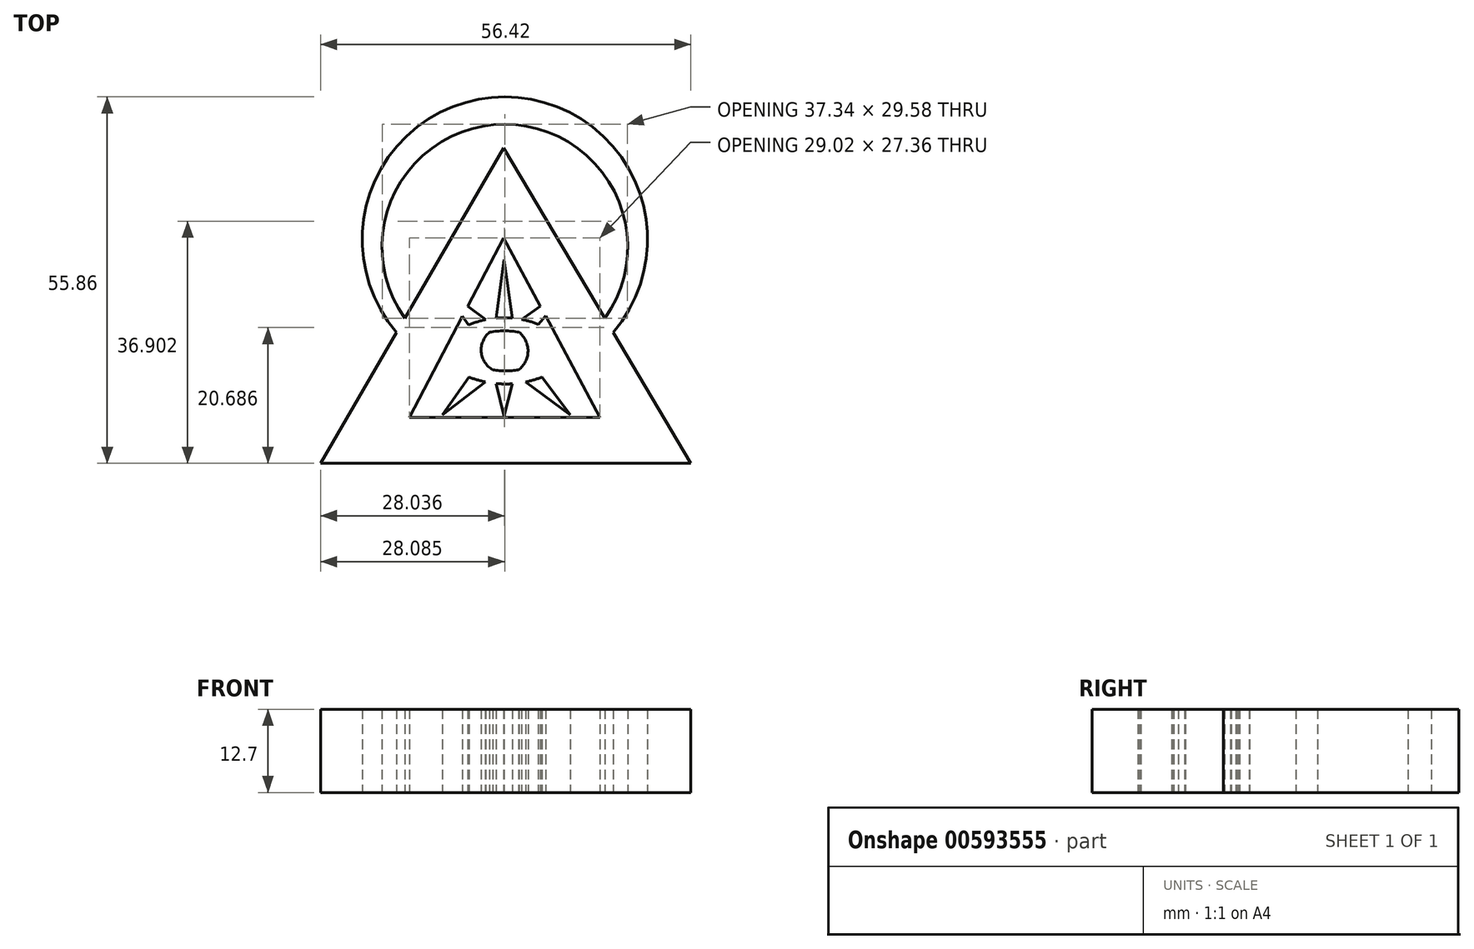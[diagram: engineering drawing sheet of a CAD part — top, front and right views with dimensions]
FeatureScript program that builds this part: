
annotation { "Feature Type Name" : "Feature", "Feature Type Description" : "" }
export const myFeature = defineFeature(function(context is Context, id is Id, definition is map)
    precondition{}
    {
        {
            var Q0;
            Q0=qCreatedBy(makeId("Top.planeOp"),FACE);
            var sketch = newSketch(context, id + "F0", { "sketchPlane" : qUnion([Q0])});
            skLineSegment(sketch, "E0", {"start": v(0, 38.6) * mm, "end": v(0, -34.74) * mm, "construction": true});
            skPoint(sketch, "E1", {"position": v(-16.4, 0.56) * mm});
            skPoint(sketch, "E2", {"position": v(16.6, 0.56) * mm});
            skArc(sketch, "E3", {"start": v(16.6, 0.56) * mm, "mid": v(0.1, 36.45) * mm, "end": v(-16.4, 0.56) * mm});
            skPoint(sketch, "E4", {"position": v(-15.15, 2.7) * mm});
            skPoint(sketch, "E5", {"position": v(15.34, 2.7) * mm});
            skArc(sketch, "E6", {"start": v(15.34, 2.7) * mm, "mid": v(0.1, 32.28) * mm, "end": v(-15.15, 2.7) * mm});
            skPoint(sketch, "E7", {"position": v(-28, -19.4) * mm});
            skPoint(sketch, "E8", {"position": v(28.43, -19.4) * mm});
            skPoint(sketch, "E9", {"position": v(-0.05, 28.7) * mm});
            skLineSegment(sketch, "E10", {"start": v(-28, -19.4) * mm, "end": v(-0.05, 28.7) * mm});
            skLineSegment(sketch, "E11", {"start": v(28.43, -19.4) * mm, "end": v(-0.05, 28.7) * mm});
            skLineSegment(sketch, "E12", {"start": v(-28, -19.4) * mm, "end": v(28.43, -19.4) * mm});
            skPoint(sketch, "E13", {"position": v(-0.05, 14.96) * mm});
            skPoint(sketch, "E14", {"position": v(-14.46, -12.4) * mm});
            skLineSegment(sketch, "E15", {"start": v(-0.05, 14.96) * mm, "end": v(-14.46, -12.4) * mm});
            skPoint(sketch, "E16", {"position": v(14.56, -12.4) * mm});
            skLineSegment(sketch, "E17", {"start": v(-14.46, -12.4) * mm, "end": v(14.56, -12.4) * mm});
            skLineSegment(sketch, "E18", {"start": v(-0.05, 14.96) * mm, "end": v(14.56, -12.4) * mm});
            skLineSegment(sketch, "E19", {"start": v(-0.05, 28.7) * mm, "end": v(-0.05, 14.96) * mm, "construction": true});
            skLineSegment(sketch, "E20", {"start": v(-23.93, -12.4) * mm, "end": v(24.29, -12.4) * mm, "construction": true});
            skArc(sketch, "E21", {"start": v(-9.81, -3.57) * mm, "mid": v(0.03, -7.32) * mm, "end": v(9.97, -3.8) * mm});
            skArc(sketch, "E22", {"start": v(7.68, 0.48) * mm, "mid": v(0, 2.77) * mm, "end": v(-7.68, 0.48) * mm});
            skArc(sketch, "E23", {"start": v(-8.17, -2.18) * mm, "mid": v(0.1, -5.32) * mm, "end": v(8.43, -2.36) * mm});
            skArc(sketch, "E24", {"start": v(8.43, -2.36) * mm, "mid": v(0.16, 0.77) * mm, "end": v(-8.17, -2.18) * mm});
            skPoint(sketch, "E25", {"position": v(-1.72, -5.17) * mm});
            skPoint(sketch, "E26", {"position": v(2.2, -5.17) * mm});
            skPoint(sketch, "E27", {"position": v(2.27, 0.58) * mm});
            skArc(sketch, "E28", {"start": v(-2.22, 0.58) * mm, "mid": v(-3.49, -2.43) * mm, "end": v(-1.72, -5.17) * mm});
            skPoint(sketch, "E29", {"position": v(-2.22, 0.58) * mm});
            skArc(sketch, "E30", {"start": v(2.2, -5.17) * mm, "mid": v(3.63, -2.32) * mm, "end": v(2.27, 0.58) * mm});
            skLineSegment(sketch, "E31", {"start": v(-2.88, -7) * mm, "end": v(-9.45, -12.05) * mm});
            skLineSegment(sketch, "E32", {"start": v(-9.45, -12.05) * mm, "end": v(-5.38, -6.26) * mm});
            skLineSegment(sketch, "E33", {"start": v(3.3, -7) * mm, "end": v(10.06, -12.01) * mm});
            skLineSegment(sketch, "E34", {"start": v(10.06, -12.01) * mm, "end": v(5.8, -6.27) * mm});
            skLineSegment(sketch, "E35", {"start": v(-6.35, 3) * mm, "end": v(-5.42, 1.68) * mm});
            skLineSegment(sketch, "E36", {"start": v(-5.53, 4.55) * mm, "end": v(-2.82, 2.49) * mm});
            skLineSegment(sketch, "E37", {"start": v(-1.25, 2.72) * mm, "end": v(0, 11.63) * mm});
            skLineSegment(sketch, "E38", {"start": v(0, 11.63) * mm, "end": v(1.25, 2.72) * mm});
            skLineSegment(sketch, "E39", {"start": v(2.67, 2.52) * mm, "end": v(5.51, 4.53) * mm});
            skLineSegment(sketch, "E40", {"start": v(6.3, 3.05) * mm, "end": v(5.21, 1.77) * mm});
            skLineSegment(sketch, "E41", {"start": v(-7.68, 0.48) * mm, "end": v(-9.81, -3.57) * mm});
            skLineSegment(sketch, "E42", {"start": v(-6.35, 3) * mm, "end": v(-5.53, 4.55) * mm});
            skLineSegment(sketch, "E43", {"start": v(7.68, 0.48) * mm, "end": v(9.97, -3.8) * mm});
            skLineSegment(sketch, "E44", {"start": v(5.51, 4.53) * mm, "end": v(6.3, 3.05) * mm});
            skArc(sketch, "E45", {"start": v(2.27, 0.58) * mm, "mid": v(0.03, 0.77) * mm, "end": v(-2.22, 0.58) * mm});
            skLineSegment(sketch, "E46", {"start": v(-1.25, -7.25) * mm, "end": v(0, -12.25) * mm});
            skLineSegment(sketch, "E47", {"start": v(0, -12.25) * mm, "end": v(1.25, -7.29) * mm});
            skLineSegment(sketch, "E48", {"start": v(0, -12.25) * mm, "end": v(-1.25, -7.25) * mm, "construction": true});
            skLineSegment(sketch, "E49", {"start": v(-1.25, 2.72) * mm, "end": v(-1.25, -9.07) * mm, "construction": true});
            skLineSegment(sketch, "E50", {"start": v(1.25, 2.72) * mm, "end": v(1.25, -9.05) * mm, "construction": true});
            skSolve(sketch);
        }
        {
            var Q0;
            Q0 = qSketchRegion(id + "F0", true);
            var Q1;
            {var subQ0=sQuery(id+"F0.wireOp",EDGE,"E28");Q1=makeQuery(id+"F0.imprint","IMPRINT",FACE,{"disambiguationData":[TD([[makeQuery(id+"F0.imprint","IMPRINT",EDGE,{"derivedFrom":subQ0}),1.0]])]});}
            var Q2;
            {var subQ10=sQuery(id+"F0.wireOp",EDGE,"E41");Q2=makeQuery(id+"F0.imprint","IMPRINT",FACE,{"disambiguationData":[TD([[makeQuery(id+"F0.imprint","IMPRINT",EDGE,{"derivedFrom":subQ10}),1.0]])]});}
            var Q3;
            {var subQ0=sQuery(id+"F0.wireOp",EDGE,"E35");Q3=makeQuery(id+"F0.imprint","IMPRINT",FACE,{"disambiguationData":[TD([[makeQuery(id+"F0.imprint","IMPRINT",EDGE,{"derivedFrom":subQ0}),1.0]])]});}
            var Q4;
            {var subQ0=sQuery(id+"F0.wireOp",EDGE,"E37");Q4=makeQuery(id+"F0.imprint","IMPRINT",FACE,{"disambiguationData":[TD([[makeQuery(id+"F0.imprint","IMPRINT",EDGE,{"derivedFrom":subQ0}),-1.0]])]});}
            var Q5;
            {var subQ0=sQuery(id+"F0.wireOp",EDGE,"E39");Q5=makeQuery(id+"F0.imprint","IMPRINT",FACE,{"disambiguationData":[TD([[makeQuery(id+"F0.imprint","IMPRINT",EDGE,{"derivedFrom":subQ0}),-1.0]])]});}
            var Q6;
            {var subQ0=sQuery(id+"F0.wireOp",EDGE,"E31");Q6=makeQuery(id+"F0.imprint","IMPRINT",FACE,{"disambiguationData":[TD([[makeQuery(id+"F0.imprint","IMPRINT",EDGE,{"derivedFrom":subQ0}),-1.0]])]});}
            var Q7;
            {var subQ0=sQuery(id+"F0.wireOp",EDGE,"E33");Q7=makeQuery(id+"F0.imprint","IMPRINT",FACE,{"disambiguationData":[TD([[makeQuery(id+"F0.imprint","IMPRINT",EDGE,{"derivedFrom":subQ0}),1.0]])]});}
            var Q8;
            {var subQ0=sQuery(id+"F0.wireOp",EDGE,"E46");Q8=makeQuery(id+"F0.imprint","IMPRINT",FACE,{"disambiguationData":[TD([[makeQuery(id+"F0.imprint","IMPRINT",EDGE,{"derivedFrom":subQ0}),1.0]])]});}
            var Q9;
            Q9=sQuery(id+"F0.wireOp",EDGE,"E3");
            var Q10;
            Q10=sQuery(id+"F0.wireOp",EDGE,"E6");
            var Q11;
            Q11=sQuery(id+"F0.wireOp",EDGE,"E10");
            var Q12;
            Q12=sQuery(id+"F0.wireOp",EDGE,"E12");
            var Q13;
            Q13=sQuery(id+"F0.wireOp",EDGE,"E17");
            var Q14;
            Q14=sQuery(id+"F0.wireOp",EDGE,"E15");
            var Q15;
            Q15=sQuery(id+"F0.wireOp",EDGE,"E18");
            var Q16;
            Q16=sQuery(id+"F0.wireOp",EDGE,"E11");
            var Q17;
            Q17=sQuery(id+"F0.wireOp",EDGE,"E31");
            var Q18;
            Q18=sQuery(id+"F0.wireOp",EDGE,"E32");
            var Q19;
            Q19=sQuery(id+"F0.wireOp",EDGE,"cENFgDZo-e2X2-sVkA-bZeN-yT4mE3rmpJwd");
            var Q20;
            Q20=sQuery(id+"F0.wireOp",EDGE,"vWQVmkAs-JZlU-UwJa-lEx6-7OVIaMs9nSNG");
            var Q21;
            Q21=sQuery(id+"F0.wireOp",EDGE,"E33");
            var Q22;
            Q22=sQuery(id+"F0.wireOp",EDGE,"E34");
            var Q23;
            Q23=sQuery(id+"F0.wireOp",EDGE,"E21");
            var Q24;
            Q24=sQuery(id+"F0.wireOp",EDGE,"E23");
            var Q25;
            Q25=sQuery(id+"F0.wireOp",EDGE,"E30");
            var Q26;
            Q26=sQuery(id+"F0.wireOp",EDGE,"E28");
            var Q27;
            Q27=sQuery(id+"F0.wireOp",EDGE,"E24");
            var Q28;
            Q28=sQuery(id+"F0.wireOp",EDGE,"E35");
            var Q29;
            Q29=sQuery(id+"F0.wireOp",EDGE,"E36");
            var Q30;
            Q30=sQuery(id+"F0.wireOp",EDGE,"E22");
            var Q31;
            Q31=sQuery(id+"F0.wireOp",EDGE,"E37");
            var Q32;
            Q32=sQuery(id+"F0.wireOp",EDGE,"E38");
            var Q33;
            Q33=sQuery(id+"F0.wireOp",EDGE,"E39");
            var Q34;
            Q34=sQuery(id+"F0.wireOp",EDGE,"E40");
            extrude(context, id + "F1", {"entities" : qUnion([Q0, Q1, Q2, Q3, Q4, Q5, Q6, Q7, Q8]), "surfaceEntities" : qUnion([Q9, Q10, Q11, Q12, Q13, Q14, Q15, Q16, Q17, Q18, Q19, Q20, Q21, Q22, Q23, Q24, Q25, Q26, Q27, Q28, Q29, Q30, Q31, Q32, Q33, Q34]), "depth" : 12.7 * mm, "offsetDistance" : 25 * mm});
        }
    });
